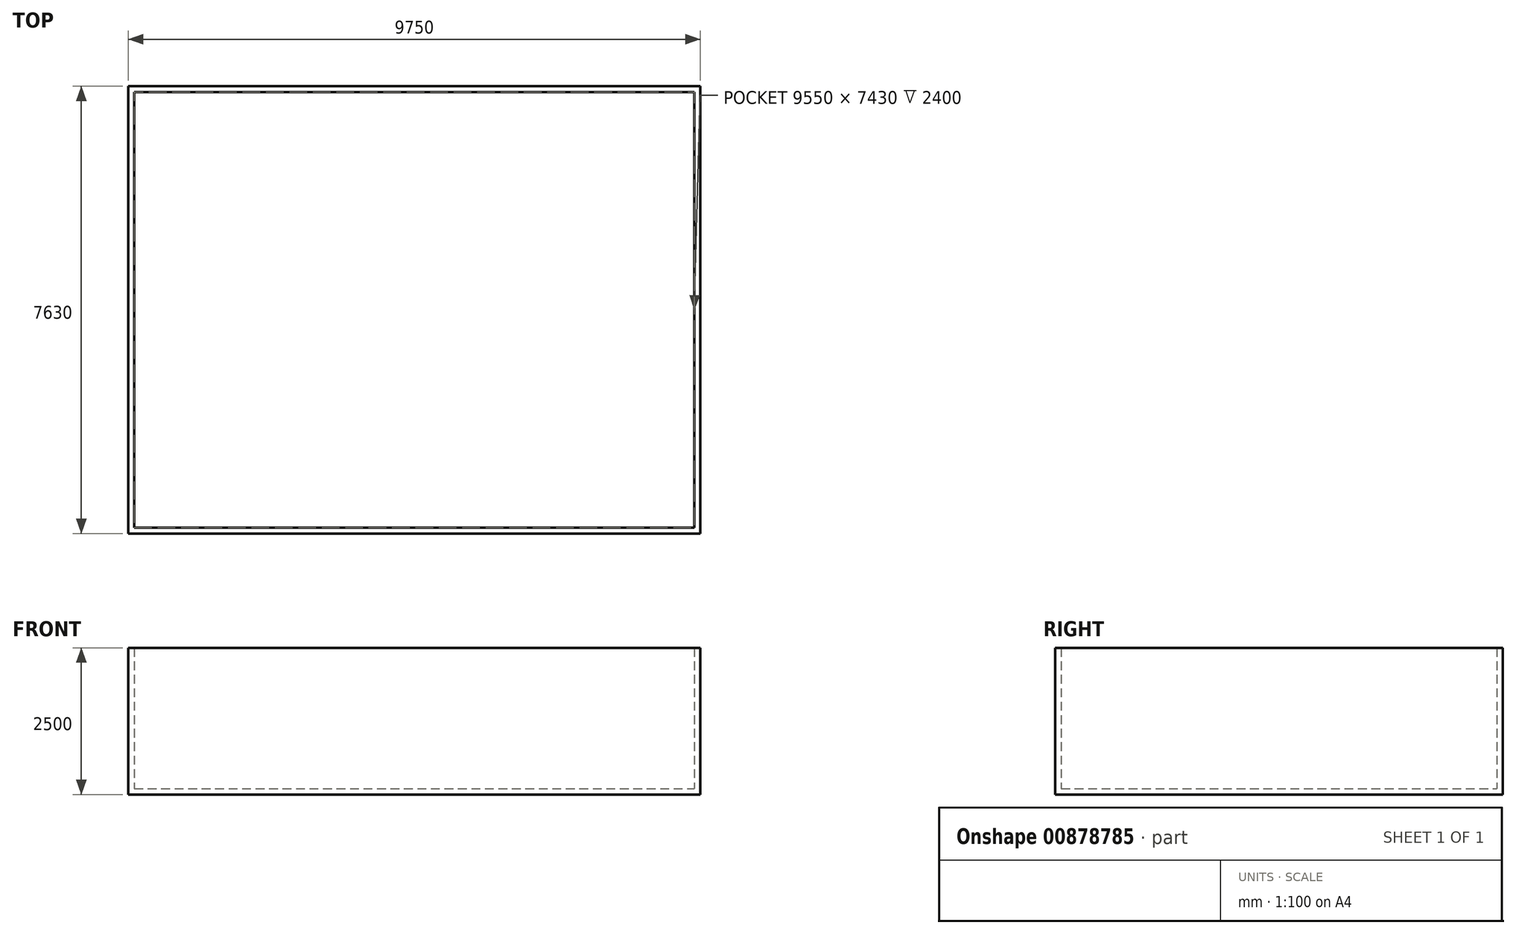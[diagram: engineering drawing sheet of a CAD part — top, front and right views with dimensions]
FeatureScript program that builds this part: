
annotation { "Feature Type Name" : "Feature", "Feature Type Description" : "" }
export const myFeature = defineFeature(function(context is Context, id is Id, definition is map)
    precondition{}
    {
        {
            var Q0;
            Q0=qCreatedBy(makeId("Top.planeOp"),FACE);
            var sketch = newSketch(context, id + "F0", { "sketchPlane" : qUnion([Q0])});
            skLineSegment(sketch, "E0.bottom", {"start": v(0, 0) * mm, "end": v(9750, 0) * mm});
            skLineSegment(sketch, "E0.left", {"start": v(0, 0) * mm, "end": v(0, 7630) * mm});
            skLineSegment(sketch, "E0.right", {"start": v(9750, 0) * mm, "end": v(9750, 7630) * mm});
            skLineSegment(sketch, "E1", {"start": v(0, 7630) * mm, "end": v(9750, 7630) * mm});
            skSolve(sketch);
        }
        {
            var Q0;
            Q0 = qSketchRegion(id + "F0", true);
            extrude(context, id + "F1", {"entities" : qUnion([Q0]), "depth" : 2500 * mm, "offsetDistance" : 25 * mm});
        }
        {
            var Q0;
            Q0=makeQuery(id+"F1.opExtrude","CAP_FACE",FACE,{"disambiguationData":[OSD([sQuery(id+"F0.wireOp",EDGE,"E0.bottom"),sQuery(id+"F0.wireOp",EDGE,"E0.left"),sQuery(id+"F0.wireOp",EDGE,"E0.right"),sQuery(id+"F0.wireOp",EDGE,"E1")])],"isStart":false});
            shell(context, id + "F2", {"entities" : qUnion([Q0]), "thickness" : 100 * mm});
        }
        {
            var Q0;
            Q0=makeQuery(id+"F2.opShell","OFFSET_FACE",FACE,{"disambiguationData":[OSD([sQuery(id+"F0.wireOp",EDGE,"E0.bottom"),sQuery(id+"F0.wireOp",EDGE,"E0.left"),sQuery(id+"F0.wireOp",EDGE,"E0.right"),sQuery(id+"F0.wireOp",EDGE,"E1")])]});
            var sketch = newSketch(context, id + "F3", { "sketchPlane" : qUnion([Q0])});
            skLineSegment(sketch, "E2", {"start": v(2960, 7530) * mm, "end": v(2960, 4030) * mm});
            skLineSegment(sketch, "E3", {"start": v(2960, 4030) * mm, "end": v(100, 4030) * mm});
            skLineSegment(sketch, "E4", {"start": v(2960, 4030) * mm, "end": v(4410, 4030) * mm});
            skLineSegment(sketch, "E5", {"start": v(4410, 4030) * mm, "end": v(4410, 7530) * mm});
            skSolve(sketch);
        }
        {
            var Q0;
            {var subQ0=sQuery(id+"F3.wireOp",EDGE,"E2");Q0=makeQuery(id+"F3.imprint","IMPRINT",FACE,{"disambiguationData":[TD([[makeQuery(id+"F3.imprint","IMPRINT",EDGE,{"derivedFrom":subQ0}),-1.0]])]});}
            var Q1;
            Q1=sQuery(id+"F3.wireOp",EDGE,"E2");
            var Q2;
            Q2=sQuery(id+"F3.wireOp",EDGE,"E3");
            var Q3;
            Q3=sQuery(id+"F3.wireOp",EDGE,"E5");
            extrude(context, id + "F4", {"entities" : qUnion([Q0]), "bodyType" : ToolBodyType.SURFACE, "operationType" : NewBodyOperationType.REMOVE, "surfaceEntities" : qUnion([Q1, Q2, Q3]), "depth" : 2400 * mm, "offsetDistance" : 25 * mm});
        }
    });
